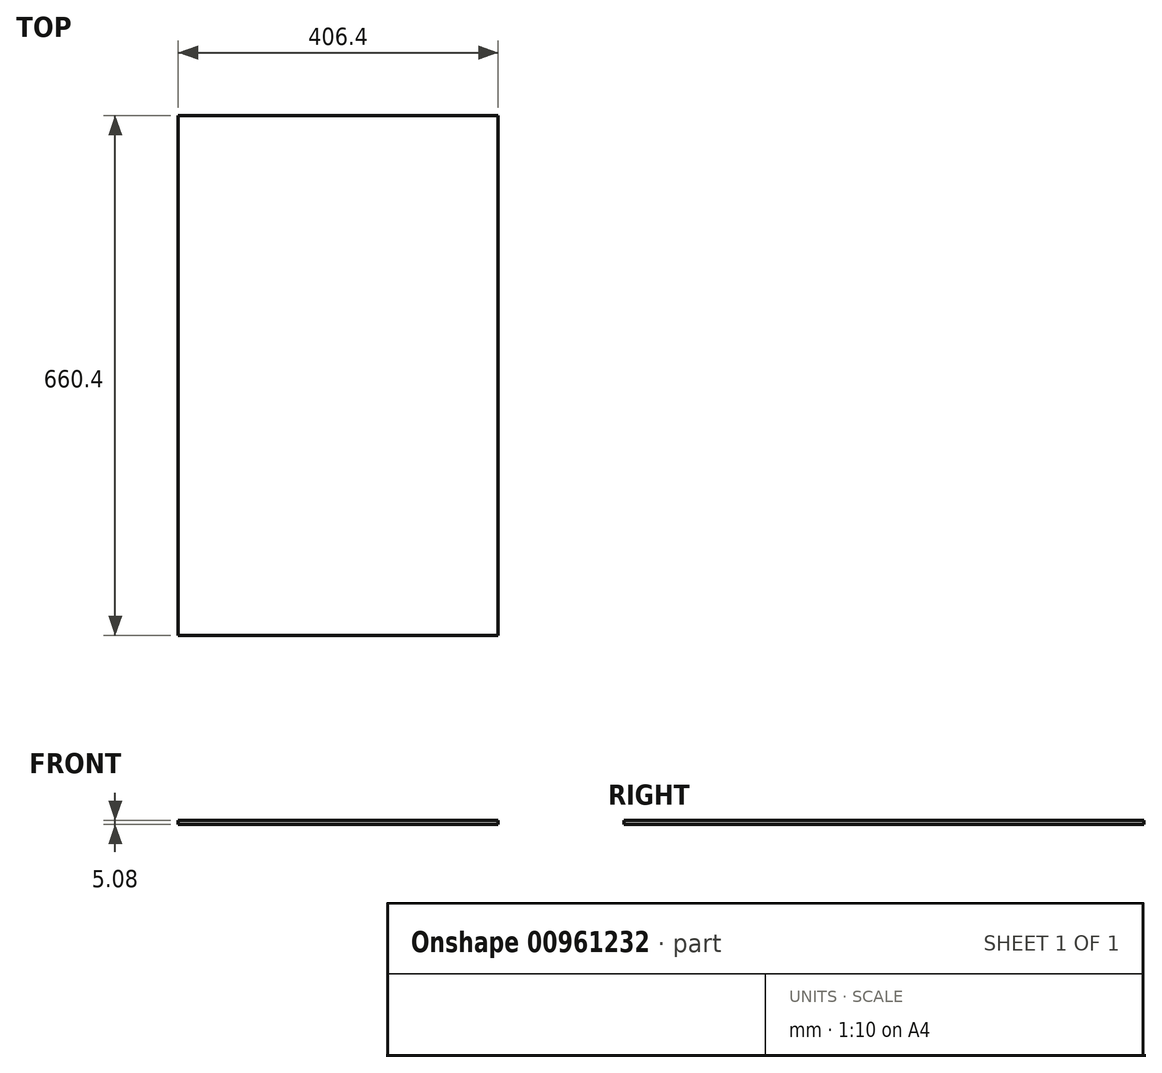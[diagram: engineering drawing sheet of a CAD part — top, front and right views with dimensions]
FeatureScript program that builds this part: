
annotation { "Feature Type Name" : "Feature", "Feature Type Description" : "" }
export const myFeature = defineFeature(function(context is Context, id is Id, definition is map)
    precondition{}
    {
        {
            var Q0;
            Q0=qCreatedBy(makeId("Top.planeOp"),FACE);
            var sketch = newSketch(context, id + "F0", { "sketchPlane" : qUnion([Q0])});
            skLineSegment(sketch, "E0.bottom", {"start": v(203.2, 330.2) * mm, "end": v(-203.2, 330.2) * mm});
            skLineSegment(sketch, "E0.top", {"start": v(203.2, -330.2) * mm, "end": v(-203.2, -330.2) * mm});
            skLineSegment(sketch, "E0.left", {"start": v(203.2, 330.2) * mm, "end": v(203.2, -330.2) * mm});
            skLineSegment(sketch, "E0.right", {"start": v(-203.2, 330.2) * mm, "end": v(-203.2, -330.2) * mm});
            skPoint(sketch, "E0.middle", {"position": v(0, 0) * mm});
            skSolve(sketch);
        }
        {
            var Q0;
            Q0=makeQuery(id+"F0.imprint","IMPRINT",FACE,{"disambiguationData":[TD([[makeQuery(id+"F0.imprint","IMPRINT",EDGE,{"derivedFrom":sQuery(id+"F0.wireOp",EDGE,"E0.bottom")}),1.0]])]});
            extrude(context, id + "F1", {"entities" : qUnion([Q0]), "depth" : 5.08 * mm, "offsetDistance" : 25.4 * mm});
        }
    });
